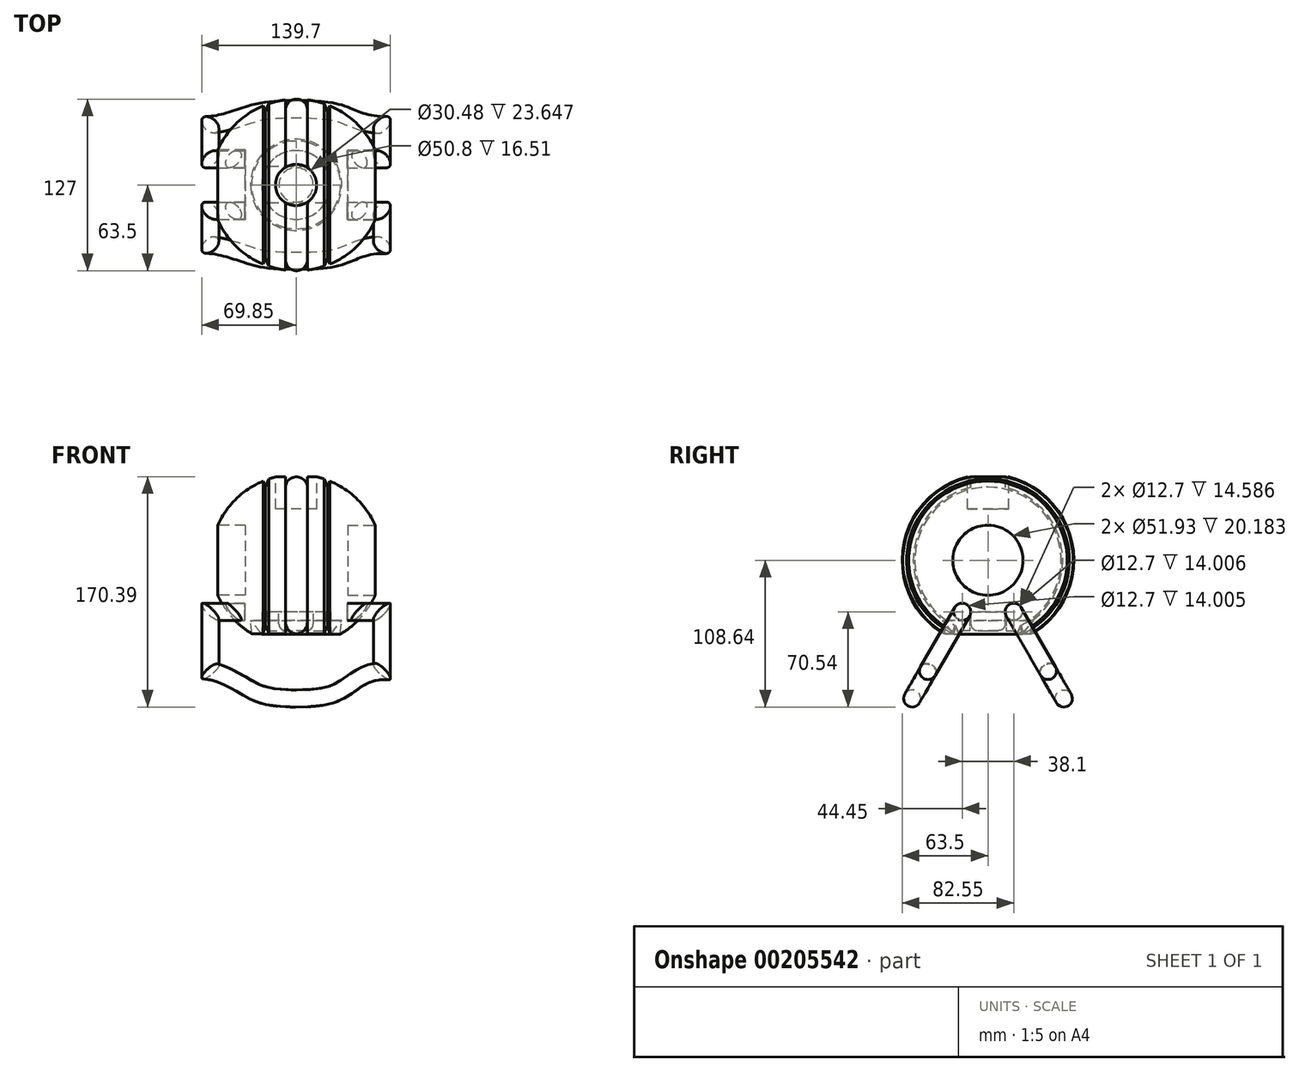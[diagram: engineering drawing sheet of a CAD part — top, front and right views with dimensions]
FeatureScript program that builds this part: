
annotation { "Feature Type Name" : "Feature", "Feature Type Description" : "" }
export const myFeature = defineFeature(function(context is Context, id is Id, definition is map)
    precondition{}
    {
        {
            var Q0;
            Q0=qCreatedBy(makeId("Top.planeOp"),FACE);
            var sketch = newSketch(context, id + "F0", { "sketchPlane" : qUnion([Q0])});
            skLineSegment(sketch, "E0", {"start": v(0, 0) * mm, "end": v(25.77, 0) * mm});
            skArc(sketch, "E1", {"start": v(127.3, 0) * mm, "mid": v(105.7, 47.7) * mm, "end": v(55.62, 62.97) * mm});
            skLineSegment(sketch, "E2", {"start": v(5.58, 25.97) * mm, "end": v(25.77, 25.97) * mm});
            skLineSegment(sketch, "E3", {"start": v(25.77, 25.97) * mm, "end": v(25.77, 0) * mm});
            skLineSegment(sketch, "E4", {"start": v(63.8, 0) * mm, "end": v(63.8, 55.33) * mm});
            skArc(sketch, "E5", {"start": v(5.58, 25.97) * mm, "mid": v(1.42, 13.28) * mm, "end": v(0, 0) * mm});
            skLineSegment(sketch, "E6", {"start": v(25.77, 0) * mm, "end": v(127.3, 0) * mm});
            skLineSegment(sketch, "E7", {"start": v(55.62, 63.13) * mm, "end": v(55.62, 55.33) * mm});
            skLineSegment(sketch, "E8", {"start": v(55.62, 55.33) * mm, "end": v(63.8, 55.33) * mm, "construction": true});
            skArc(sketch, "E9", {"start": v(55.62, 62.97) * mm, "mid": v(25.76, 51.02) * mm, "end": v(5.58, 25.97) * mm});
            skLineSegment(sketch, "E10", {"start": v(63.8, 55.33) * mm, "end": v(63.8, 63.5) * mm});
            skArc(sketch, "E11", {"start": v(55.62, 55.33) * mm, "mid": v(58.01, 61.1) * mm, "end": v(63.8, 63.5) * mm});
            skLineSegment(sketch, "E12", {"start": v(43.45, 60.21) * mm, "end": v(40.85, 54.1) * mm});
            skLineSegment(sketch, "E13", {"start": v(40.85, 54.1) * mm, "end": v(39.05, 58.56) * mm});
            skSolve(sketch);
        }
        {
            var Q0;
            {var subQ4=sQuery(id+"F0.wireOp",EDGE,"E2");Q0=makeQuery(id+"F0.imprint","IMPRINT",FACE,{"disambiguationData":[TD([[makeQuery(id+"F0.imprint","IMPRINT",EDGE,{"derivedFrom":subQ4}),1.0]])]});}
            var Q1;
            Q1=sQuery(id+"F0.wireOp",EDGE,"E6");
            revolve(context, id + "F1", {"entities" : qUnion([Q0]), "axis" : qUnion([Q1]), "revolveType" : RevolveType.FULL});
        }
        {
            var Q0;
            Q0=makeQuery(id+"F1.opRevolve","SWEPT_BODY",BODY,{"disambiguationData":[OSD([sQuery(id+"F0.wireOp",EDGE,"E2"),sQuery(id+"F0.wireOp",EDGE,"E3"),sQuery(id+"F0.wireOp",EDGE,"E4"),sQuery(id+"F0.wireOp",EDGE,"E6"),sQuery(id+"F0.wireOp",EDGE,"E7"),sQuery(id+"F0.wireOp",EDGE,"E9"),sQuery(id+"F0.wireOp",EDGE,"E10"),sQuery(id+"F0.wireOp",EDGE,"E11"),sQuery(id+"F0.wireOp",EDGE,"E12"),sQuery(id+"F0.wireOp",EDGE,"E13")])]});
            var Q1;
            Q1=makeQuery(id+"F1.opRevolve","SWEPT_FACE",FACE,{"disambiguationData":[OSD([sQuery(id+"F0.wireOp",EDGE,"E4"),sQuery(id+"F0.wireOp",EDGE,"E10")])]});
            mirror(context, id + "F2", {"operationType" : NewBodyOperationType.ADD, "entities" : qUnion([Q0]), "mirrorPlane" : qUnion([Q1])});
        }
        {
            var Q0;
            Q0=qCreatedBy(makeId("Top.planeOp"),FACE);
            cPlane(context, id + "F3", {"entities" : qUnion([Q0]), "cplaneType" : CPlaneType.OFFSET, "offset" : 63.5 * mm, "width" : 152.4 * mm, "height" : 152.4 * mm});
        }
        {
            var Q0;
            Q0=qCreatedBy(id+"F3.planeOp",FACE);
            var sketch = newSketch(context, id + "F4", { "sketchPlane" : qUnion([Q0])});
            skPoint(sketch, "E14", {"position": v(63.5, 0) * mm});
            skPoint(sketch, "E15.0", {"position": v(0, 0) * mm});
            skCircle(sketch, "E16", {"center": v(63.5, 0) * mm, "radius": 15.24 * mm});
            skSolve(sketch);
        }
        {
            var Q0;
            Q0=makeQuery(id+"F4.imprint","IMPRINT",FACE,{"disambiguationData":[TD([[makeQuery(id+"F4.imprint","IMPRINT",EDGE,{"derivedFrom":sQuery(id+"F4.wireOp",EDGE,"E16")}),1.0]])]});
            extrude(context, id + "F5", {"entities" : qUnion([Q0]), "operationType" : NewBodyOperationType.REMOVE, "oppositeDirection" : true, "depth" : 25.4 * mm});
        }
        {
            var Q0;
            Q0=qCreatedBy(makeId("Top.planeOp"),FACE);
            cPlane(context, id + "F6", {"entities" : qUnion([Q0]), "cplaneType" : CPlaneType.OFFSET, "offset" : 63.5 * mm, "oppositeDirection" : true, "width" : 152.4 * mm, "height" : 152.4 * mm});
        }
        {
            var Q0;
            Q0=qCreatedBy(id+"F6.planeOp",FACE);
            var sketch = newSketch(context, id + "F7", { "sketchPlane" : qUnion([Q0])});
            skPoint(sketch, "E17.0", {"position": v(63.5, 0) * mm});
            skCircle(sketch, "E18", {"center": v(63.5, 0) * mm, "radius": 31.75 * mm});
            skCircle(sketch, "E19", {"center": v(63.5, 0) * mm, "radius": 25.4 * mm});
            skSolve(sketch);
        }
        {
            var Q0;
            Q0=makeQuery(id+"F7.imprint","IMPRINT",FACE,{"disambiguationData":[TD([[makeQuery(id+"F7.imprint","IMPRINT",EDGE,{"derivedFrom":sQuery(id+"F7.wireOp",EDGE,"E18")}),1.0]])]});
            extrude(context, id + "F8", {"entities" : qUnion([Q0]), "operationType" : NewBodyOperationType.REMOVE, "depth" : 19.05 * mm, "hasDraft" : true, "draftAngle" : 6 * degree});
        }
        {
            var Q0;
            Q0=makeQuery(id+"F7.imprint","IMPRINT",FACE,{"disambiguationData":[TD([[makeQuery(id+"F7.imprint","IMPRINT",EDGE,{"derivedFrom":sQuery(id+"F7.wireOp",EDGE,"E19")}),1.0]])]});
            extrude(context, id + "F9", {"entities" : qUnion([Q0]), "operationType" : NewBodyOperationType.REMOVE, "depth" : 25.4 * mm});
        }
        {
            var Q0;
            Q0=qCreatedBy(makeId("Right.planeOp"),FACE);
            cPlane(context, id + "F10", {"entities" : qUnion([Q0]), "cplaneType" : CPlaneType.OFFSET, "offset" : 63.5 * mm, "width" : 152.4 * mm, "height" : 152.4 * mm});
        }
        {
            var Q0;
            Q0=qCreatedBy(id+"F10.planeOp",FACE);
            var sketch = newSketch(context, id + "F11", { "sketchPlane" : qUnion([Q0])});
            skLineSegment(sketch, "E20", {"start": v(-33.75, -44.45) * mm, "end": v(-25.4, -44.45) * mm});
            skLineSegment(sketch, "E21", {"start": v(-25.4, -44.45) * mm, "end": v(-25.4, -54.61) * mm});
            skLineSegment(sketch, "E22", {"start": v(-25.4, -54.61) * mm, "end": v(-33.75, -44.45) * mm});
            skSolve(sketch);
        }
        {
            var Q0;
            Q0=makeQuery(id+"F11.imprint","IMPRINT",FACE,{"disambiguationData":[TD([[makeQuery(id+"F11.imprint","IMPRINT",EDGE,{"derivedFrom":sQuery(id+"F11.wireOp",EDGE,"E20")}),-1.0]])]});
            var Q1;
            Q1=sQuery(id+"F4.wireOp",EDGE,"E16");
            revolve(context, id + "F12", {"operationType" : NewBodyOperationType.ADD, "entities" : qUnion([Q0]), "axis" : qUnion([Q1]), "revolveType" : RevolveType.FULL});
        }
        {
            var Q0;
            Q0=qCreatedBy(id+"F6.planeOp",FACE);
            var Q1;
            Q1=sQuery(id+"F11.wireOp",VERTEX,"E22.start");
            cPlane(context, id + "F13", {"entities" : qUnion([Q0, Q1]), "cplaneType" : CPlaneType.PLANE_POINT, "offset" : 25.4 * mm, "width" : 152.4 * mm, "height" : 152.4 * mm});
        }
        {
            var Q0;
            Q0=qCreatedBy(id+"F13.planeOp",FACE);
            var sketch = newSketch(context, id + "F14", { "sketchPlane" : qUnion([Q0])});
            skPoint(sketch, "E23.0", {"position": v(63.5, 0) * mm});
            skCircle(sketch, "E24.0", {"center": v(63.5, 0) * mm, "radius": 25.4 * mm});
            skLineSegment(sketch, "E25", {"start": v(41.98, -13.5) * mm, "end": v(85.02, -13.5) * mm});
            skLineSegment(sketch, "E26", {"start": v(41.98, 13.5) * mm, "end": v(85.02, 13.5) * mm});
            skPoint(sketch, "E27", {"position": v(63.5, 13.5) * mm});
            skPoint(sketch, "E28", {"position": v(63.5, -13.5) * mm});
            skSolve(sketch);
        }
        {
            var Q0;
            {var subQ0=sQuery(id+"F14.wireOp",EDGE,"E26");Q0=makeQuery(id+"F14.imprint","IMPRINT",FACE,{"disambiguationData":[TD([[makeQuery(id+"F14.imprint","IMPRINT",EDGE,{"derivedFrom":subQ0}),1.0]])]});}
            var Q1;
            {var subQ0=sQuery(id+"F14.wireOp",EDGE,"E25");Q1=makeQuery(id+"F14.imprint","IMPRINT",FACE,{"disambiguationData":[TD([[makeQuery(id+"F14.imprint","IMPRINT",EDGE,{"derivedFrom":subQ0}),-1.0]])]});}
            extrude(context, id + "F15", {"entities" : qUnion([Q0, Q1]), "operationType" : NewBodyOperationType.ADD, "depth" : 25.4 * mm, "hasSecondDirection" : true, "secondDirectionOppositeDirection" : false, "secondDirectionDepth" : 2.54 * mm});
        }
        {
            var Q0;
            Q0=makeQuery(id+"F9.boolean.opBoolean","COPY",FACE,{"derivedFrom":makeQuery(id+"F9.opExtrude","CAP_FACE",FACE,{"disambiguationData":[OSD([sQuery(id+"F7.wireOp",EDGE,"E19")])],"isStart":false})});
            var sketch = newSketch(context, id + "F16", { "sketchPlane" : qUnion([Q0])});
            skPoint(sketch, "E29.0", {"position": v(63.5, 0) * mm});
            skCircle(sketch, "E30", {"center": v(63.5, 0) * mm, "radius": 12.7 * mm});
            skPoint(sketch, "E31.0", {"position": v(63.5, 13.5) * mm});
            skSolve(sketch);
        }
        {
            var Q0;
            Q0 = qSketchRegion(id + "F16", true);
            var Q1;
            Q1=makeQuery(id+"F15.opExtrude","CAP_FACE",FACE,{"disambiguationData":[OSD([sQuery(id+"F14.wireOp",EDGE,"E24.0"),sQuery(id+"F14.wireOp",EDGE,"E25")])],"isStart":true});
            extrude(context, id + "F17", {"entities" : qUnion([Q0]), "operationType" : NewBodyOperationType.ADD, "endBound" : BoundingType.UP_TO_SURFACE, "endBoundEntityFace" : qUnion([Q1]), "depth" : 25.4 * mm});
        }
        {
            var Q0;
            Q0=makeQuery(id+"F17.opExtrude","CAP_FACE",FACE,{"disambiguationData":[OSD([sQuery(id+"F16.wireOp",EDGE,"E30")])],"isStart":false});
            fillet(context, id + "F18", {"entities" : qUnion([Q0]), "radius" : 5.08 * mm, "tangentPropagation" : true, "allowEdgeOverflow" : false});
        }
        {
            var Q0;
            Q0=qCreatedBy(makeId("Right.planeOp"),FACE);
            var sketch = newSketch(context, id + "F19", { "sketchPlane" : qUnion([Q0])});
            skCircle(sketch, "E32", {"center": v(-19.05, -38.1) * mm, "radius": 6.35 * mm});
            skCircle(sketch, "E33", {"center": v(19.05, -38.1) * mm, "radius": 6.35 * mm});
            skLineSegment(sketch, "E34", {"start": v(0, 0) * mm, "end": v(0, -38.1) * mm, "construction": true});
            skLineSegment(sketch, "E35", {"start": v(-19.05, -38.1) * mm, "end": v(19.05, -38.1) * mm, "construction": true});
            skSolve(sketch);
        }
        {
            var Q0;
            Q0 = qSketchRegion(id + "F19", true);
            extrude(context, id + "F20", {"entities" : qUnion([Q0]), "operationType" : NewBodyOperationType.REMOVE, "depth" : 25.4 * mm});
        }
        {
            var Q0;
            Q0=makeQuery(id+"F20.boolean.opBoolean","COPY",FACE,{"derivedFrom":makeQuery(id+"F20.opExtrude","CAP_FACE",FACE,{"disambiguationData":[OSD([sQuery(id+"F19.wireOp",EDGE,"E32")])],"isStart":false})});
            var Q1;
            Q1=makeQuery(id+"F20.boolean.opBoolean","COPY",FACE,{"derivedFrom":makeQuery(id+"F20.opExtrude","SWEPT_FACE",FACE,{"disambiguationData":[OSD([sQuery(id+"F19.wireOp",EDGE,"E32")])]})});
            var Q2;
            Q2=makeQuery(id+"F20.boolean.opBoolean","COPY",FACE,{"derivedFrom":makeQuery(id+"F20.opExtrude","CAP_FACE",FACE,{"disambiguationData":[OSD([sQuery(id+"F19.wireOp",EDGE,"E33")])],"isStart":false})});
            var Q3;
            Q3=makeQuery(id+"F20.boolean.opBoolean","COPY",FACE,{"derivedFrom":makeQuery(id+"F20.opExtrude","SWEPT_FACE",FACE,{"disambiguationData":[OSD([sQuery(id+"F19.wireOp",EDGE,"E33")])]})});
            var Q4;
            Q4=qCreatedBy(id+"F10.planeOp",FACE);
            mirror(context, id + "F21", {"patternType" : MirrorType.FACE, "faces" : qUnion([Q0, Q1, Q2, Q3]), "mirrorPlane" : qUnion([Q4])});
        }
        {
            var Q0;
            Q0=qCreatedBy(makeId("Front.planeOp"),FACE);
            cPlane(context, id + "F22", {"entities" : qUnion([Q0]), "cplaneType" : CPlaneType.OFFSET, "offset" : 19.05 * mm, "width" : 152.4 * mm, "height" : 152.4 * mm});
        }
        {
            var Q0;
            Q0=qCreatedBy(id+"F22.planeOp",FACE);
            var sketch = newSketch(context, id + "F23", { "sketchPlane" : qUnion([Q0])});
            skLineSegment(sketch, "E36.0", {"start": v(25.4, -31.75) * mm, "end": v(25.4, -44.45) * mm, "construction": true});
            skPoint(sketch, "E37", {"position": v(25.4, -38.1) * mm});
            skLineSegment(sketch, "E38.0.0", {"start": v(101.6, -31.75) * mm, "end": v(101.6, -44.45) * mm, "construction": true});
            skPoint(sketch, "E39", {"position": v(101.6, -38.1) * mm});
            skLineSegment(sketch, "E40", {"start": v(101.6, -38.1) * mm, "end": v(127, -38.1) * mm});
            skLineSegment(sketch, "E41", {"start": v(127, -38.1) * mm, "end": v(127, -88.9) * mm});
            skLineSegment(sketch, "E42", {"start": v(127, -88.9) * mm, "end": v(0, -88.9) * mm, "construction": true});
            skLineSegment(sketch, "E43", {"start": v(0, -88.9) * mm, "end": v(0, -38.1) * mm});
            skLineSegment(sketch, "E44", {"start": v(0, -38.1) * mm, "end": v(25.4, -38.1) * mm});
            skFitSpline(sketch, "E45", {"points": [v(127, -88.9) * mm, v(101.6, -101.7) * mm, v(84.14, -110.43) * mm, v(43.45, -110.43) * mm, v(25.4, -101.7) * mm, v(0, -88.9) * mm], "startDerivative": vector(-172.35, -4.98) * mm, "endDerivative": vector(-110.7, 15.13) * mm});
            skPoint(sketch, "E46", {"position": v(63.5, -88.9) * mm});
            skPoint(sketch, "E47.0", {"position": v(84.14, -54.62) * mm});
            skPoint(sketch, "E47.1", {"position": v(43.45, -54.38) * mm});
            skSolve(sketch);
        }
        {
            var Q0;
            Q0=makeQuery(id+"F21.opPattern","COPY",FACE,{"derivedFrom":makeQuery(id+"F20.boolean.opBoolean","COPY",FACE,{"derivedFrom":makeQuery(id+"F20.opExtrude","CAP_FACE",FACE,{"disambiguationData":[OSD([sQuery(id+"F19.wireOp",EDGE,"E32")])],"isStart":false})}),"instanceName":"1"});
            var Q1;
            Q1=sQuery(id+"F23.wireOp",EDGE,"E40");
            var Q2;
            Q2=sQuery(id+"F23.wireOp",EDGE,"E41");
            var Q3;
            Q3=sQuery(id+"F23.wireOp",EDGE,"E45");
            var Q4;
            Q4=sQuery(id+"F23.wireOp",EDGE,"E43");
            var Q5;
            Q5=sQuery(id+"F23.wireOp",EDGE,"E44");
            sweep(context, id + "F24", {"profiles" : qUnion([Q0]), "path" : qUnion([Q1, Q2, Q3, Q4, Q5])});
        }
        {
            var Q0;
            Q0=makeQuery(id+"F24.opSweep","SWEPT_BODY",BODY,{"disambiguationData":[OSD([sQuery(id+"F19.wireOp",EDGE,"E32"),sQuery(id+"F23.wireOp",EDGE,"E44")])]});
            var Q1;
            Q1=sQuery(id+"F19.wireOp",EDGE,"E32");
            transform(context, id + "F25", {"entities" : qUnion([Q0]), "transformType" : TransformType.ROTATION, "transformAxis" : qUnion([Q1]), "angle" : 30 * degree, "oppositeDirection" : true, "makeCopy" : false});
        }
        {
            var Q0;
            Q0=makeQuery(id+"F24.opSweep","SWEPT_BODY",BODY,{"disambiguationData":[OSD([sQuery(id+"F19.wireOp",EDGE,"E32"),sQuery(id+"F23.wireOp",EDGE,"E44")])]});
            var Q1;
            Q1=qCreatedBy(makeId("Front.planeOp"),FACE);
            mirror(context, id + "F26", {"entities" : qUnion([Q0]), "mirrorPlane" : qUnion([Q1])});
        }
    });
